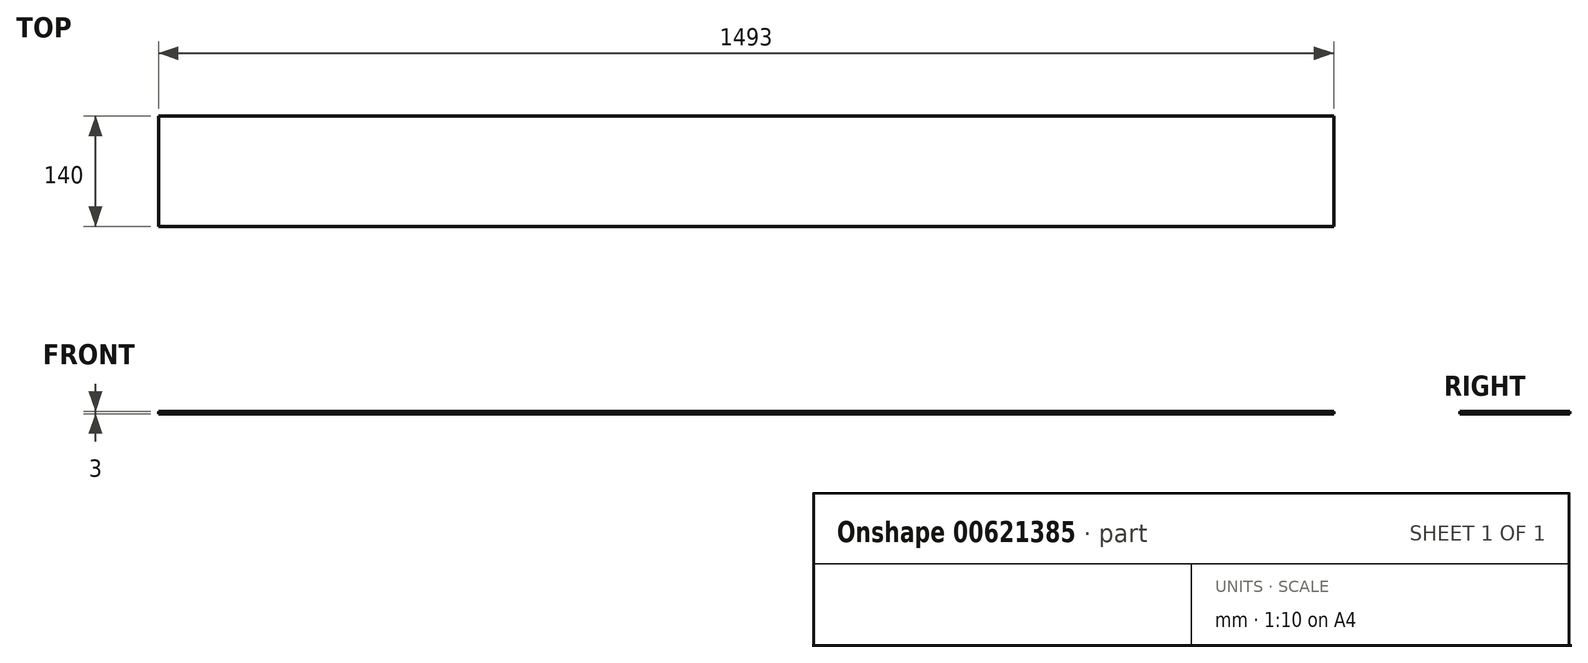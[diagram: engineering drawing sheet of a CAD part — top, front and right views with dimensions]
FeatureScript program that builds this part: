
annotation { "Feature Type Name" : "Feature", "Feature Type Description" : "" }
export const myFeature = defineFeature(function(context is Context, id is Id, definition is map)
    precondition{}
    {
        {
            var Q0;
            Q0=qCreatedBy(makeId("Top.planeOp"), FACE);
            var sketch = newSketch(context, id + "F0", { "sketchPlane" : qUnion([Q0])});
            skLineSegment(sketch, "E0.bottom", {"start": v(746.5, -70) * mm, "end": v(-746.5, -70) * mm});
            skLineSegment(sketch, "E0.top", {"start": v(746.5, 70) * mm, "end": v(-746.5, 70) * mm});
            skLineSegment(sketch, "E0.left", {"start": v(746.5, -70) * mm, "end": v(746.5, 70) * mm});
            skLineSegment(sketch, "E0.right", {"start": v(-746.5, -70) * mm, "end": v(-746.5, 70) * mm});
            skPoint(sketch, "E0.middle", {"position": v(0, 0) * mm});
            skSolve(sketch);
        }
        {
            var Q0;
            Q0 = qSketchRegion(id + "F0", true);
            extrude(context, id + "F1", {"entities" : qUnion([Q0]), "depth" : 3 * mm, "offsetDistance" : 25 * mm});
        }
    });
